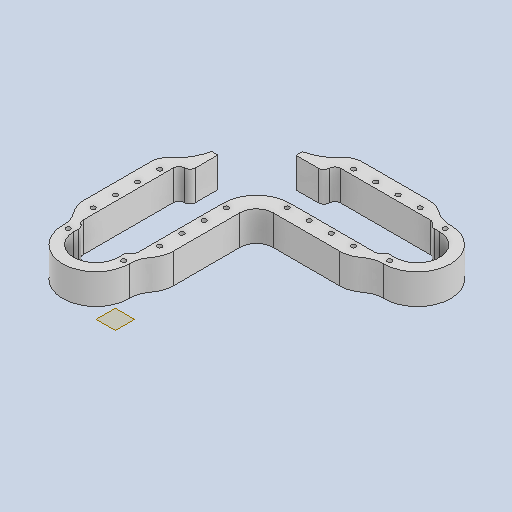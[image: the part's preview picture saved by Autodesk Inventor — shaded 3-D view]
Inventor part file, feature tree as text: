
AUTODESK INVENTOR PART (.ipt)
format: ipt  version: 2025.1 (Build 291241020, 241B)  size: 278,016 bytes
history: native  units: in
note: dims shown in document units (in); Inventor stores cm internally (conversion verified against a paired STEP export)
features: plane x1, extrude x1, sketch x1
ambient origin geometry x8: Origin, YZ Plane, XZ Plane, XY Plane, X Axis, Y Axis, Z Axis, Center Point
bodies: Solid1 (feature_tree)
feature tree (3):
  plane  "Work Plane1"
  extrude  "Extrusion2"  Depth=0.25in
  sketch  "Sketch2"  dims[d55=1.355in d56=0.0in d62=0.2087in d64=0.2832in d65=1.0084in d72=0.5in d73=0.75in d74=0.75in d75=0.2528in d76=1.0in d77=1.0in d78=1.0in d104=0.25in d105=0.25in d106=0.25in d107=0.25in d109=0.25in d110=0.25in d111=0.75in d112=0.75in d114=1.375in d115=1.25in d116=1.0in d117=1.0in d118=1.0in d122=1.5in d124=0.2087in d125=0.25in d126=0.25in d127=0.25in d128=0.2357in d129=0.5in d130=0.75in d131=0.75in d132=0.6687in d133=0.25in d134=3.817in d135=0.2165in d136=1.0in d137=4.0379in d138=11.282in d139=1.0in d140=0.2357in d141=0.5in d142=0.5in d143=0.75in d144=0.75in d145=0.5in d146=1.0in d147=0.75in d148=1.0in d149=1.0in d150=1.0in d151=0.2087in d152=0.75in d153=0.4999in d154=0.75in d155=1.5043in d156=1.0042in d157=0.25in d158=0.25in d159=3.8254in d160=0.433in d161=0.2165in d162=0.2357in d163=0.2087in d164=1.5048in d165=0.2357in d166=0.25in d167=0.25in d168=0.433in d169=0.2087in d170=0.2087in d171=1.8433in d172=1.0084in d173=2.0in d174=0.75in d175=0.5769in d176=2.9857in d177=0.2087in d178=0.2087in d179=0.433in d180=0.2165in d181=0.125in d182=2.9857in d183=4.067in d184=0.2832in d185=1.0084in d186=2.0in d187=0.75in d188=0.25in d189=1.1798in d190=0.5655in d191=0.1898in]
